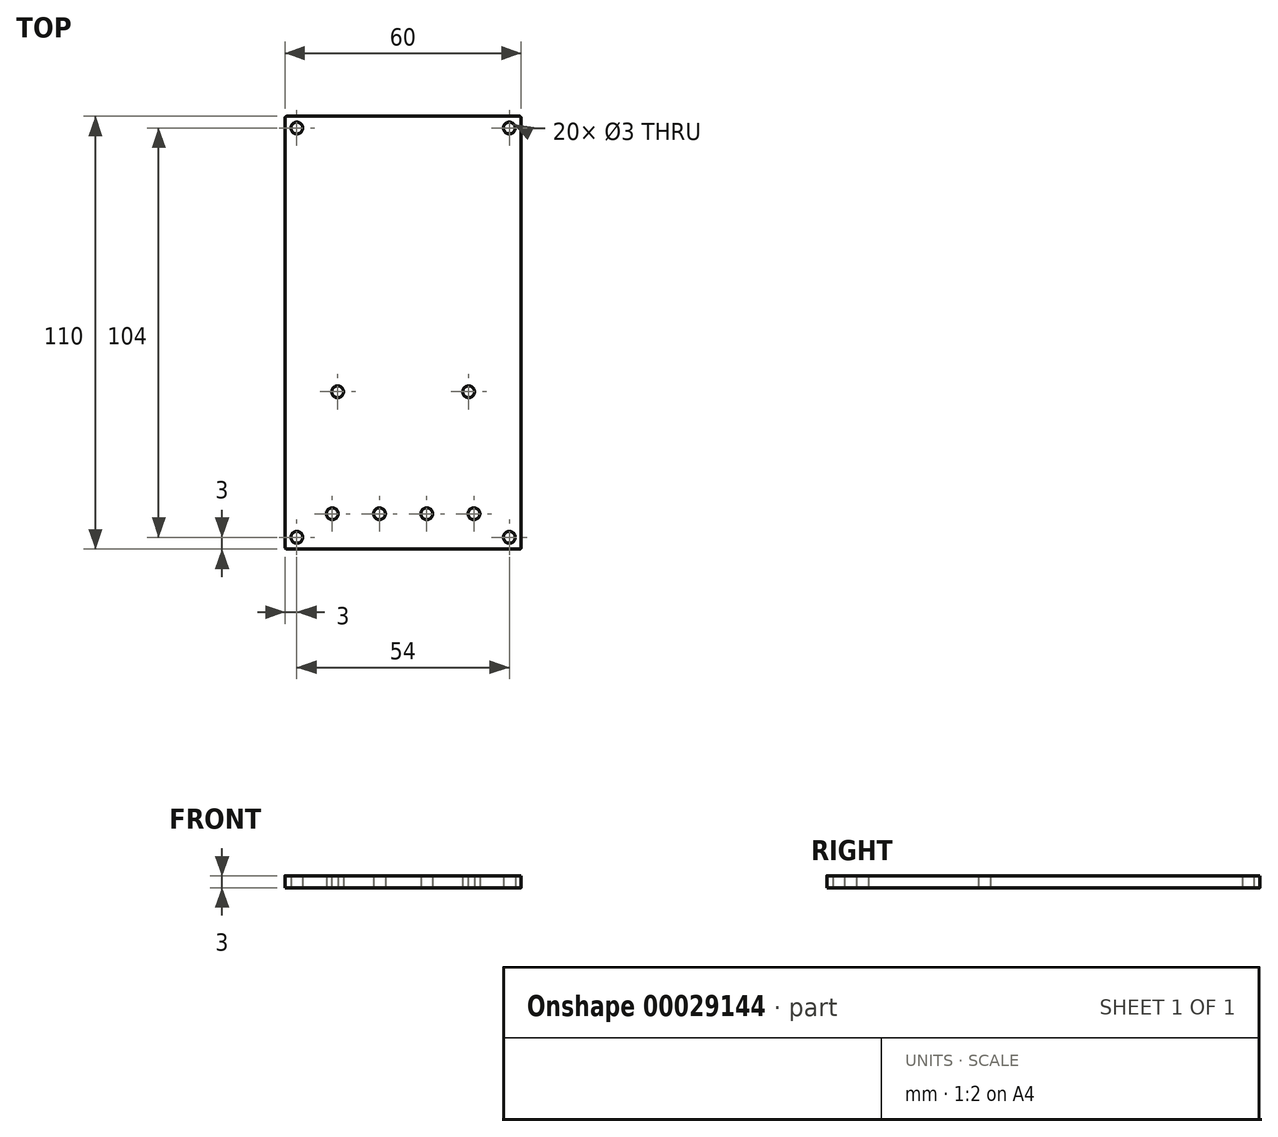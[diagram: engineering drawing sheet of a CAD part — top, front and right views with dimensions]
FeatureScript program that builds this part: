
annotation { "Feature Type Name" : "Feature", "Feature Type Description" : "" }
export const myFeature = defineFeature(function(context is Context, id is Id, definition is map)
    precondition{}
    {
        {
            var Q0;
            Q0=qCreatedBy(makeId("Top.planeOp"),FACE);
            var sketch = newSketch(context, id + "F0", { "sketchPlane" : qUnion([Q0])});
            skLineSegment(sketch, "E0.rect.bottom", {"start": v(29.5, -55) * mm, "end": v(-29.5, -55) * mm});
            skLineSegment(sketch, "E0.rect.top", {"start": v(29.5, 55) * mm, "end": v(-29.5, 55) * mm});
            skLineSegment(sketch, "E0.rect.left", {"start": v(30, -54.5) * mm, "end": v(30, 54.5) * mm});
            skLineSegment(sketch, "E0.rect.right", {"start": v(-30, -54.5) * mm, "end": v(-30, 54.5) * mm});
            skPoint(sketch, "E0.rect.middle", {"position": v(0, 0) * mm});
            skCircle(sketch, "E1", {"center": v(-27, 52) * mm, "radius": 1.5 * mm});
            skLineSegment(sketch, "E2", {"start": v(0, 55) * mm, "end": v(0, -55) * mm, "construction": true});
            skLineSegment(sketch, "E3", {"start": v(-30, 0) * mm, "end": v(30, 0) * mm, "construction": true});
            skLineSegment(sketch, "E4", {"start": v(30.94, 1.26) * mm, "end": v(30, 0) * mm, "construction": true});
            skCircle(sketch, "E5.MirrorC", {"center": v(-27, -52) * mm, "radius": 1.5 * mm});
            skCircle(sketch, "E6.MirrorC", {"center": v(27, -52) * mm, "radius": 1.5 * mm});
            skCircle(sketch, "E7.MirrorC", {"center": v(27, 52) * mm, "radius": 1.5 * mm});
            skPoint(sketch, "E8.visualSharp", {"position": v(-30, 55) * mm});
            skArc(sketch, "E8.filletArc", {"start": v(-29.5, 55) * mm, "mid": v(-29.85, 54.85) * mm, "end": v(-30, 54.5) * mm});
            skPoint(sketch, "E9.visualSharp", {"position": v(30, 55) * mm});
            skArc(sketch, "E9.filletArc", {"start": v(30, 54.5) * mm, "mid": v(29.85, 54.85) * mm, "end": v(29.5, 55) * mm});
            skPoint(sketch, "E10.visualSharp", {"position": v(30, -55) * mm});
            skArc(sketch, "E10.filletArc", {"start": v(29.5, -55) * mm, "mid": v(29.85, -54.85) * mm, "end": v(30, -54.5) * mm});
            skPoint(sketch, "E11.visualSharp", {"position": v(-30, -55) * mm});
            skArc(sketch, "E11.filletArc", {"start": v(-30, -54.5) * mm, "mid": v(-29.85, -54.85) * mm, "end": v(-29.5, -55) * mm});
            skCircle(sketch, "E12", {"center": v(16.64, -15) * mm, "radius": 1.5 * mm});
            skCircle(sketch, "E13.MirrorC", {"center": v(-16.64, -15) * mm, "radius": 1.5 * mm});
            skCircle(sketch, "E14", {"center": v(-6, -46) * mm, "radius": 1.5 * mm});
            skCircle(sketch, "E15.MirrorC", {"center": v(6, -46) * mm, "radius": 1.5 * mm});
            skCircle(sketch, "E16", {"center": v(-18, -46) * mm, "radius": 1.5 * mm});
            skCircle(sketch, "E17.MirrorC", {"center": v(18, -46) * mm, "radius": 1.5 * mm});
            skSolve(sketch);
        }
        {
            var Q0;
            Q0=makeQuery(id+"F0.imprint","IMPRINT",FACE,{"disambiguationData":[TD([[makeQuery(id+"F0.imprint","IMPRINT",EDGE,{"derivedFrom":sQuery(id+"F0.wireOp",EDGE,"E0.rect.bottom")}),-1.0]])]});
            extrude(context, id + "F1", {"entities" : qUnion([Q0]), "depth" : 3 * mm});
        }
    });
